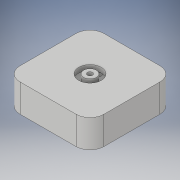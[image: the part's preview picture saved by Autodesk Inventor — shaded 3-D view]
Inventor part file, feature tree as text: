
AUTODESK INVENTOR PART (.ipt)
format: ipt  version: 2019 (Build 230136000, 136)  size: 128,512 bytes
history: native  units: in
note: dims shown in document units (in); Inventor stores cm internally (conversion verified against a paired STEP export)
features: extrude x4, sketch x3, fillet x1
ambient origin geometry x8: Origin, YZ Plane, XZ Plane, XY Plane, X Axis, Y Axis, Z Axis, Center Point
bodies: Solid1 (feature_tree)
feature tree (8):
  extrude  "Extrusion1"  Depth=0.75in
  sketch  "Sketch2"  dims[d2=0.375in d3=0.375in]
  extrude  "Extrusion2"  Depth=0.375in
  extrude  "Extrusion3"  Depth=0.125in
  extrude  "Extrusion4"  Depth=0.125in
  fillet  "Fillet1"  Radius=0.045in
  sketch  "Sketch1"  dims[d0=0.75in d1=0.75in]
  sketch  "Sketch3"  dims[d4=0.25in d5=0.0in d6=0.1125in d7=0.2025in d8=0.045in d9=0.045in d10=0.0in d11=0.045in d12=0.0in d13=0.045in d14=0.0788in d15=0.045in d16=0.0in d17=0.125in]
